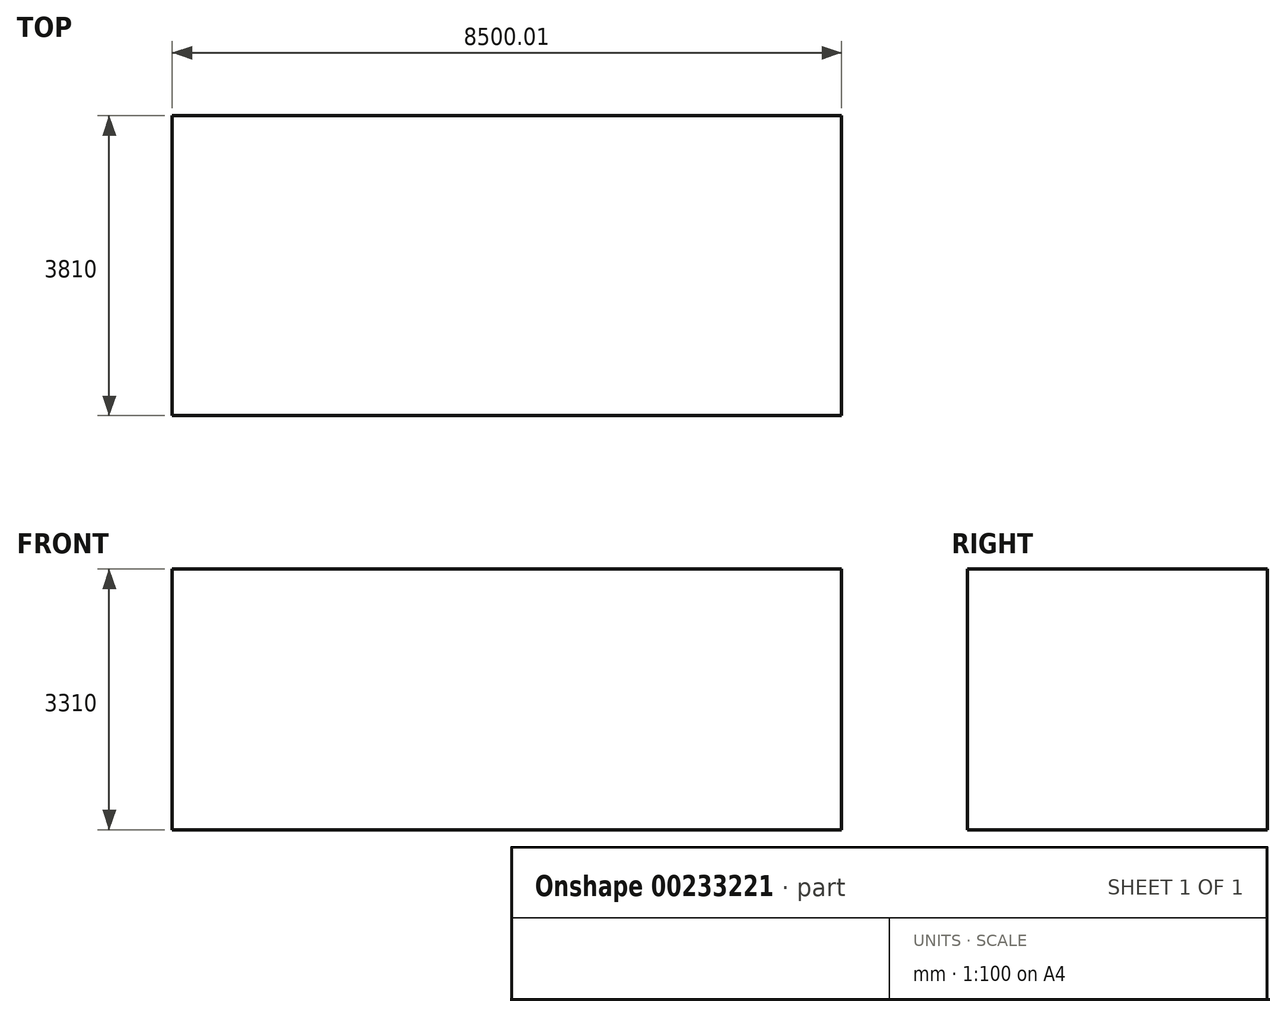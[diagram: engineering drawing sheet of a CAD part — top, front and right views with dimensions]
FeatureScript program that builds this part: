
annotation { "Feature Type Name" : "Feature", "Feature Type Description" : "" }
export const myFeature = defineFeature(function(context is Context, id is Id, definition is map)
    precondition{}
    {
        {
            var Q0;
            Q0=qCreatedBy(makeId("Front.planeOp"),FACE);
            var sketch = newSketch(context, id + "F0", { "sketchPlane" : qUnion([Q0])});
            skLineSegment(sketch, "E0.bottom", {"start": v(-4244.9, 1546.81) * mm, "end": v(4255.1, 1546.81) * mm});
            skLineSegment(sketch, "E0.top", {"start": v(-4244.9, -1763.19) * mm, "end": v(4255.1, -1763.19) * mm});
            skLineSegment(sketch, "E0.left", {"start": v(-4244.9, 1546.81) * mm, "end": v(-4244.9, -1763.19) * mm});
            skLineSegment(sketch, "E0.right", {"start": v(4255.1, 1546.81) * mm, "end": v(4255.1, -1763.19) * mm});
            skSolve(sketch);
        }
        {
            var Q0;
            Q0 = qSketchRegion(id + "F0", true);
            extrude(context, id + "F1", {"entities" : qUnion([Q0]), "depth" : 3810 * mm});
        }
    });
